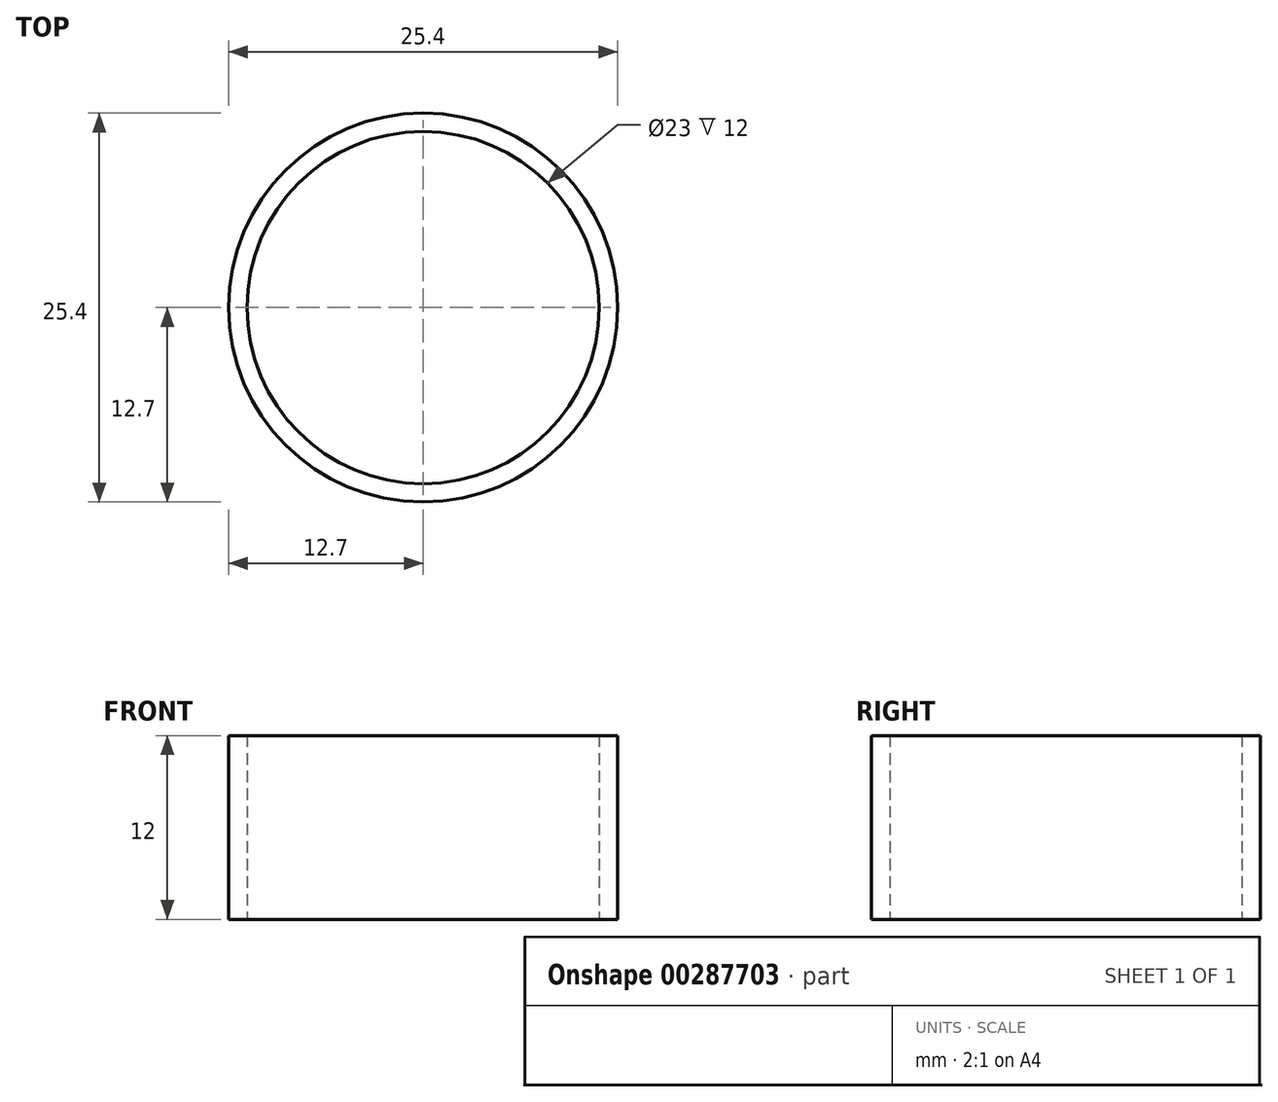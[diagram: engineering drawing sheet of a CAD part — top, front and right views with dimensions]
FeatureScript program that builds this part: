
annotation { "Feature Type Name" : "Feature", "Feature Type Description" : "" }
export const myFeature = defineFeature(function(context is Context, id is Id, definition is map)
    precondition{}
    {
        {
            var Q0;
            Q0=qCreatedBy(makeId("Top.planeOp"),FACE);
            var sketch = newSketch(context, id + "F0", { "sketchPlane" : qUnion([Q0])});
            skCircle(sketch, "E0", {"center": v(0, 0) * mm, "radius": 11.5 * mm});
            skCircle(sketch, "E1.0", {"center": v(0, 0) * mm, "radius": 12.7 * mm});
            skSolve(sketch);
        }
        {
            var Q0;
            Q0=makeQuery(id+"F0.imprint","IMPRINT",FACE,{"disambiguationData":[TD([[makeQuery(id+"F0.imprint","IMPRINT",EDGE,{"derivedFrom":sQuery(id+"F0.wireOp",EDGE,"E0")}),-1.0]])]});
            extrude(context, id + "F1", {"entities" : qUnion([Q0]), "depth" : 12 * mm});
        }
    });
